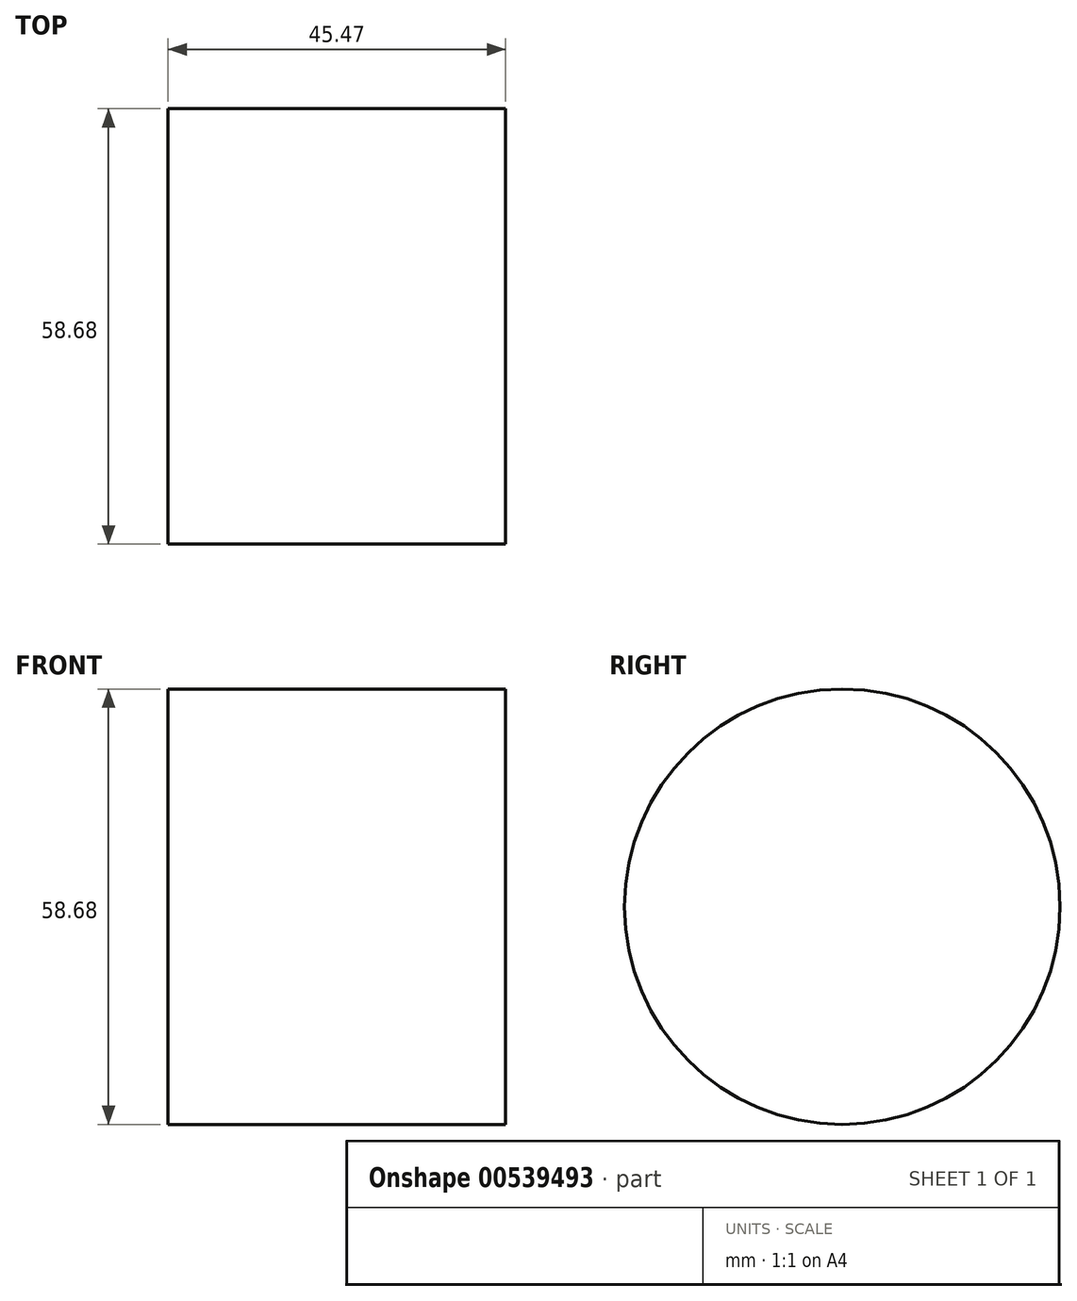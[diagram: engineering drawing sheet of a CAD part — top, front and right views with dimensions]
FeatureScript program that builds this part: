
annotation { "Feature Type Name" : "Feature", "Feature Type Description" : "" }
export const myFeature = defineFeature(function(context is Context, id is Id, definition is map)
    precondition{}
    {
        {
            var Q0;
            Q0=qCreatedBy(makeId("Right.planeOp"),FACE);
            var sketch = newSketch(context, id + "F0", { "sketchPlane" : qUnion([Q0])});
            skCircle(sketch, "E0", {"center": v(0, 0) * mm, "radius": 29.34 * mm});
            skSolve(sketch);
        }
        {
            var Q0;
            Q0 = qSketchRegion(id + "F0", true);
            var Q1;
            Q1=makeQuery(id+"F0.imprint","IMPRINT",FACE,{"disambiguationData":[TD([[makeQuery(id+"F0.imprint","IMPRINT",EDGE,{"derivedFrom":sQuery(id+"F0.wireOp",EDGE,"E0")}),1.0]])]});
            extrude(context, id + "F1", {"entities" : qUnion([Q0, Q1]), "depth" : 45.47 * mm, "offsetDistance" : 25.4 * mm});
        }
    });
